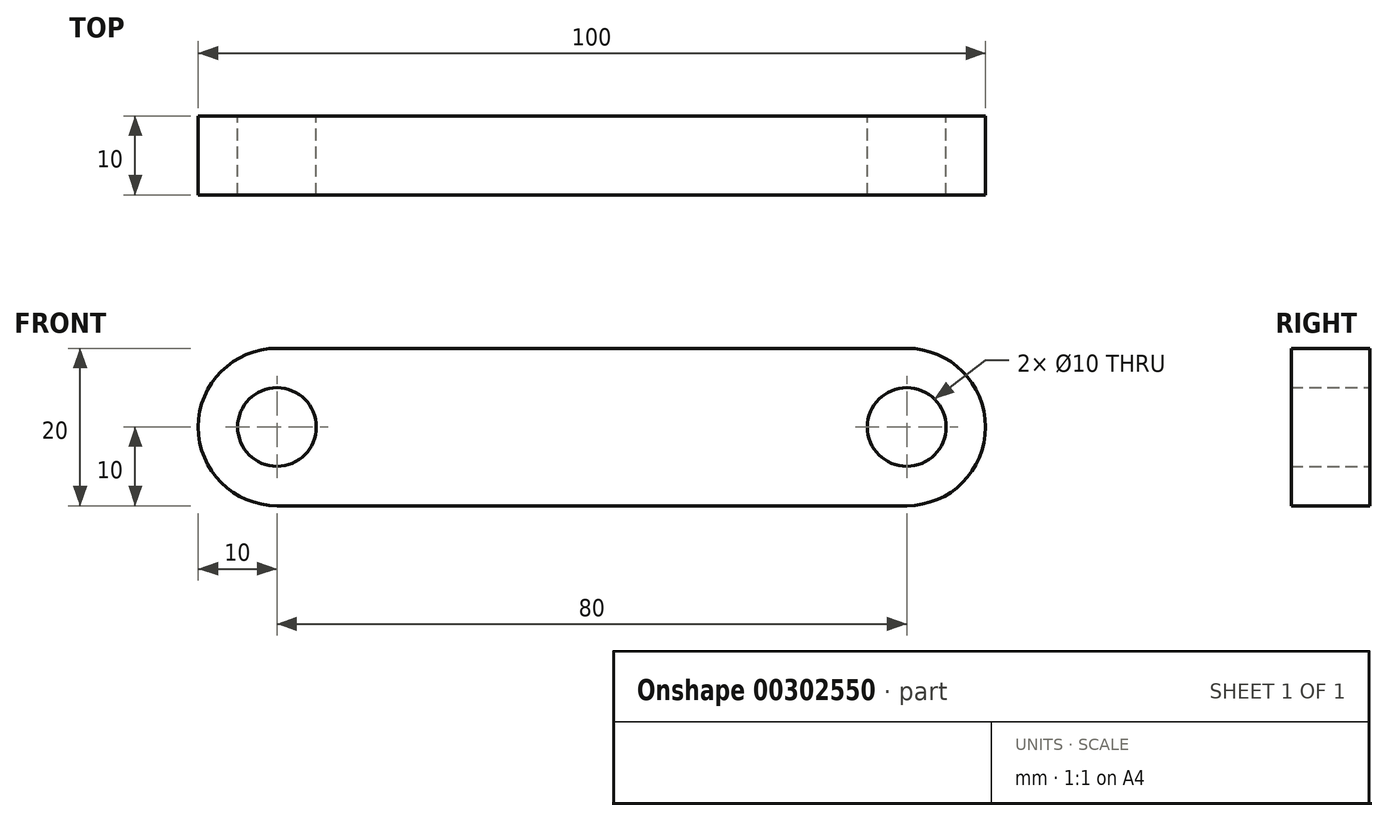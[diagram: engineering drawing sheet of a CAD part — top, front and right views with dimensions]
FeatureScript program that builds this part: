
annotation { "Feature Type Name" : "Feature", "Feature Type Description" : "" }
export const myFeature = defineFeature(function(context is Context, id is Id, definition is map)
    precondition{}
    {
        {
            var Q0;
            Q0=qCreatedBy(makeId("Front.planeOp"),FACE);
            var sketch = newSketch(context, id + "F0", { "sketchPlane" : qUnion([Q0])});
            skLineSegment(sketch, "E0.bottom", {"start": v(0, 0) * mm, "end": v(80, 0) * mm});
            skLineSegment(sketch, "E0.top", {"start": v(0, 20) * mm, "end": v(80, 20) * mm});
            skLineSegment(sketch, "E0.left", {"start": v(0, 0) * mm, "end": v(0, 20) * mm});
            skLineSegment(sketch, "E0.right", {"start": v(80, 0) * mm, "end": v(80, 20) * mm});
            skArc(sketch, "E1", {"start": v(0, 0) * mm, "mid": v(-10, 10) * mm, "end": v(0, 20) * mm});
            skArc(sketch, "E2", {"start": v(80, 0) * mm, "mid": v(90, 10) * mm, "end": v(80, 20) * mm});
            skCircle(sketch, "E3", {"center": v(0, 10) * mm, "radius": 5 * mm});
            skCircle(sketch, "E4", {"center": v(80, 10) * mm, "radius": 5 * mm});
            skSolve(sketch);
        }
        {
            var Q0;
            Q0 = qSketchRegion(id + "F0", true);
            extrude(context, id + "F1", {"entities" : qUnion([Q0]), "depth" : 10 * mm});
        }
    });
